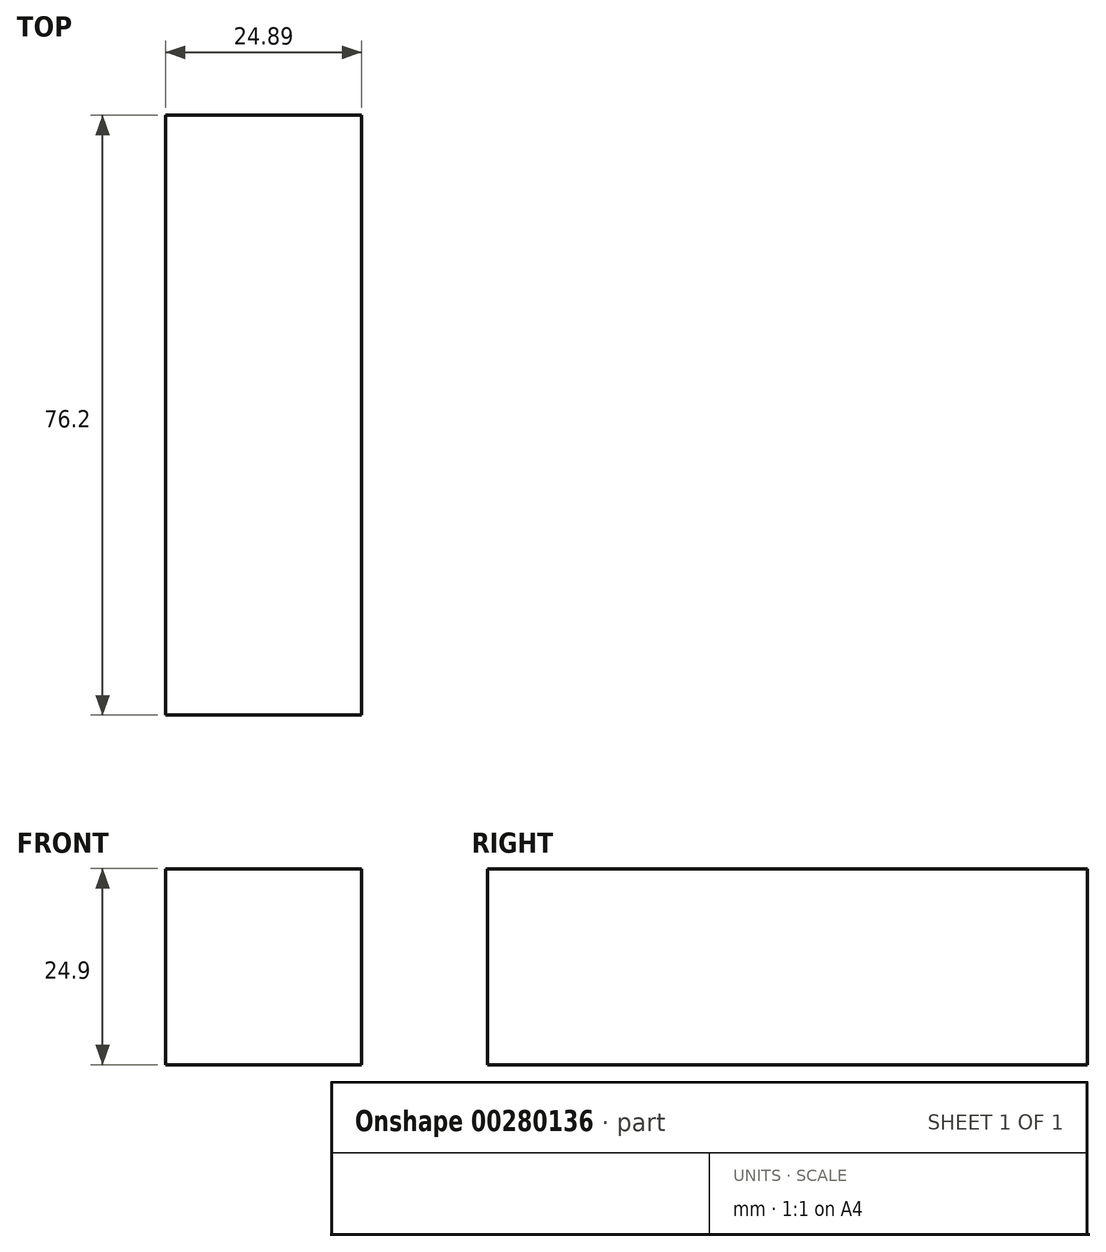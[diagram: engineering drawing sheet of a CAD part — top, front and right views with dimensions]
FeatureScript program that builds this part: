
annotation { "Feature Type Name" : "Feature", "Feature Type Description" : "" }
export const myFeature = defineFeature(function(context is Context, id is Id, definition is map)
    precondition{}
    {
        {
            var Q0;
            Q0=qCreatedBy(makeId("Front.planeOp"),FACE);
            var sketch = newSketch(context, id + "F0", { "sketchPlane" : qUnion([Q0])});
            skLineSegment(sketch, "E0.bottom", {"start": v(-53.34, 35.59) * mm, "end": v(-28.45, 35.59) * mm});
            skLineSegment(sketch, "E0.top", {"start": v(-53.34, 10.7) * mm, "end": v(-28.45, 10.7) * mm});
            skLineSegment(sketch, "E0.left", {"start": v(-53.34, 35.59) * mm, "end": v(-53.34, 10.7) * mm});
            skLineSegment(sketch, "E0.right", {"start": v(-28.45, 35.59) * mm, "end": v(-28.45, 10.7) * mm});
            skSolve(sketch);
        }
        {
            var Q0;
            Q0 = qSketchRegion(id + "F0", true);
            extrude(context, id + "F1", {"entities" : qUnion([Q0]), "depth" : 76.2 * mm});
        }
    });
